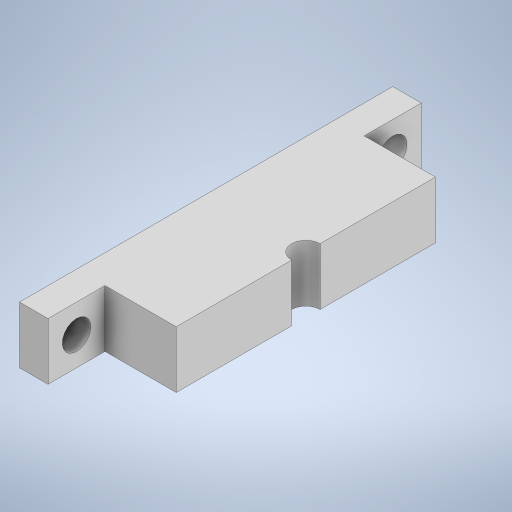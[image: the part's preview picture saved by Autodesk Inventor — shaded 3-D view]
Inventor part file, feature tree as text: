
AUTODESK INVENTOR PART (.ipt)
format: ipt  version: 2023 (Build 270158000, 158)  size: 292,352 bytes
history: native  units: mm
features: extrude x6, sketch x5
ambient origin geometry x8: Origin, YZ Plane, XZ Plane, XY Plane, X Axis, Y Axis, Z Axis, Center Point
bodies: Solid1 (feature_tree)
feature tree (11):
  sketch  "Sketch1"  dims[d0=10.0mm d1=0.0mm d2=5.0mm d3=0.0mm]
  extrude  "Extrusion1"  Depth=5.0mm TaperAngle=0.0deg
  extrude  "Extrusion2"  Depth=10.0mm TaperAngle=0.0deg
  extrude  "Extrusion4"  TaperAngle=0.0deg  [1 undecoded]
  extrude  "Extrusion5"  TaperAngle=0.0deg  [1 undecoded]
  extrude  "Extrusion6"  [1 undecoded]
  extrude  "Extrusion7"  [1 undecoded]
  sketch  "Sketch2"  dims[d4=15.0mm d7=10.0mm d8=0.0mm]
  sketch  "Sketch3"  dims[d9=5.0mm d10=0.0mm d11=0.0mm]
  sketch  "Sketch4"  dims[d12=10.0mm d13=0.0mm d14=0.0mm d15=0.0mm]
  sketch  "Sketch5"
note: 4 required parameter values undecoded (feature->parameter linkage not recoverable at this tier; creation-order binding heuristic only, values carry confidence <= 0.55)
